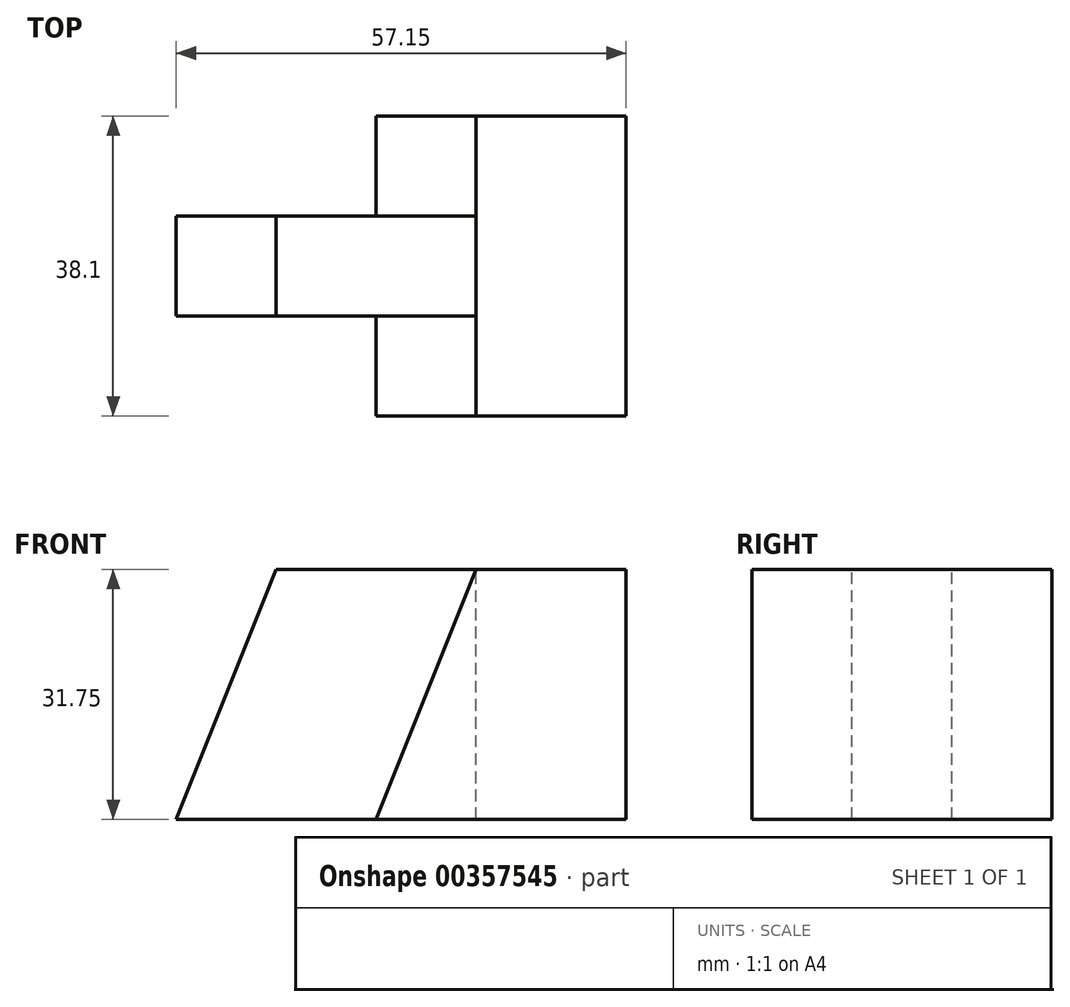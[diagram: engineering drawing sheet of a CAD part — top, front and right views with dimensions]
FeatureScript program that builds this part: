
annotation { "Feature Type Name" : "Feature", "Feature Type Description" : "" }
export const myFeature = defineFeature(function(context is Context, id is Id, definition is map)
    precondition{}
    {
        {
            var Q0;
            Q0=qCreatedBy(makeId("Front.planeOp"),FACE);
            var sketch = newSketch(context, id + "F0", { "sketchPlane" : qUnion([Q0])});
            skLineSegment(sketch, "E0", {"start": v(-42.33, 41.08) * mm, "end": v(-42.33, 9.33) * mm});
            skLineSegment(sketch, "E1", {"start": v(-42.33, 9.33) * mm, "end": v(-23.28, 9.33) * mm});
            skLineSegment(sketch, "E2", {"start": v(-23.28, 9.33) * mm, "end": v(-23.28, 41.08) * mm});
            skLineSegment(sketch, "E3", {"start": v(-23.28, 41.08) * mm, "end": v(-42.33, 41.08) * mm});
            skSolve(sketch);
        }
        {
            var Q0;
            Q0=makeQuery(id+"F0.imprint","IMPRINT",FACE,{"disambiguationData":[TD([[makeQuery(id+"F0.imprint","IMPRINT",EDGE,{"derivedFrom":sQuery(id+"F0.wireOp",EDGE,"E0")}),1.0]])]});
            extrude(context, id + "F1", {"entities" : qUnion([Q0]), "depth" : 38.1 * mm});
        }
        {
            var Q0;
            Q0=makeQuery(id+"F1.opExtrude","CAP_FACE",FACE,{"disambiguationData":[OSD([sQuery(id+"F0.wireOp",EDGE,"E0"),sQuery(id+"F0.wireOp",EDGE,"E1"),sQuery(id+"F0.wireOp",EDGE,"E2"),sQuery(id+"F0.wireOp",EDGE,"E3")])],"isStart":true});
            var sketch = newSketch(context, id + "F2", { "sketchPlane" : qUnion([Q0])});
            skLineSegment(sketch, "E4", {"start": v(42.33, 9.33) * mm, "end": v(42.33, 41.08) * mm});
            skLineSegment(sketch, "E5", {"start": v(42.33, 9.33) * mm, "end": v(55.03, 9.33) * mm});
            skLineSegment(sketch, "E6", {"start": v(55.03, 9.33) * mm, "end": v(42.33, 41.08) * mm});
            skSolve(sketch);
        }
        {
            var Q0;
            Q0 = qSketchRegion(id + "F2", true);
            extrude(context, id + "F3", {"entities" : qUnion([Q0]), "oppositeDirection" : true, "depth" : 12.7 * mm});
        }
        {
            var Q0;
            Q0=makeQuery(id+"F1.opExtrude","CAP_FACE",FACE,{"disambiguationData":[OSD([sQuery(id+"F0.wireOp",EDGE,"E0"),sQuery(id+"F0.wireOp",EDGE,"E1"),sQuery(id+"F0.wireOp",EDGE,"E2"),sQuery(id+"F0.wireOp",EDGE,"E3")])],"isStart":false});
            var sketch = newSketch(context, id + "F4", { "sketchPlane" : qUnion([Q0])});
            skLineSegment(sketch, "E7", {"start": v(-42.33, 41.08) * mm, "end": v(-42.33, 9.33) * mm});
            skLineSegment(sketch, "E8", {"start": v(-42.33, 9.33) * mm, "end": v(-55.03, 9.33) * mm});
            skLineSegment(sketch, "E9", {"start": v(-55.03, 9.33) * mm, "end": v(-42.33, 41.08) * mm});
            skSolve(sketch);
        }
        {
            var Q0;
            Q0=makeQuery(id+"F4.imprint","IMPRINT",FACE,{"disambiguationData":[TD([[makeQuery(id+"F4.imprint","IMPRINT",EDGE,{"derivedFrom":sQuery(id+"F4.wireOp",EDGE,"E7")}),-1.0]])]});
            extrude(context, id + "F5", {"entities" : qUnion([Q0]), "operationType" : NewBodyOperationType.ADD, "oppositeDirection" : true, "depth" : 12.7 * mm});
        }
        {
            var Q0;
            Q0=makeQuery(id+"F1.opExtrude","SWEPT_FACE",FACE,{"disambiguationData":[OSD([sQuery(id+"F0.wireOp",EDGE,"E3")])]});
            var sketch = newSketch(context, id + "F6", { "sketchPlane" : qUnion([Q0])});
            skLineSegment(sketch, "E10", {"start": v(-42.33, -12.7) * mm, "end": v(-67.73, -12.7) * mm});
            skLineSegment(sketch, "E11", {"start": v(-42.33, -25.4) * mm, "end": v(-42.33, -12.7) * mm});
            skLineSegment(sketch, "E12", {"start": v(-42.33, -25.4) * mm, "end": v(-67.73, -25.4) * mm});
            skLineSegment(sketch, "E13", {"start": v(-67.73, -25.4) * mm, "end": v(-67.73, -12.7) * mm});
            skSolve(sketch);
        }
        {
            var Q0;
            Q0 = qSketchRegion(id + "F6", true);
            extrude(context, id + "F7", {"entities" : qUnion([Q0]), "oppositeDirection" : true, "depth" : 31.75 * mm});
        }
        {
            var Q0;
            Q0=makeQuery(id+"F7.opExtrude","SWEPT_FACE",FACE,{"disambiguationData":[OSD([sQuery(id+"F6.wireOp",EDGE,"E10")])]});
            var sketch = newSketch(context, id + "F8", { "sketchPlane" : qUnion([Q0])});
            skLineSegment(sketch, "E14", {"start": v(67.73, 41.08) * mm, "end": v(67.73, 9.33) * mm});
            skLineSegment(sketch, "E15", {"start": v(67.73, 9.33) * mm, "end": v(80.43, 9.33) * mm});
            skLineSegment(sketch, "E16", {"start": v(67.73, 41.08) * mm, "end": v(80.43, 9.33) * mm});
            skSolve(sketch);
        }
        {
            var Q0;
            Q0 = qSketchRegion(id + "F8", true);
            extrude(context, id + "F9", {"entities" : qUnion([Q0]), "operationType" : NewBodyOperationType.ADD, "oppositeDirection" : true, "depth" : 12.7 * mm});
        }
    });
